# Revit family: BathrobeHolder-Single-Vitra-MinimaxSeries-A44787
name_source: partatom
category: Plumbing Fixtures
revit_build: Autodesk Revit 2017 (Build: 20160225_1515(x64)
units: mm (PartAtom-declared; Revit-internal decimal feet)

## family parameters
Cut with Voids When Loaded = No
Host = Face
OmniClass Number = 23.45.05.14.99
OmniClass Title = Other Sanitary Washing Plumbing Fixtures
Part Type = Normal
Room Calculation Point = No
Round Connector Dimension = Use Diameter
Shared = Yes

## types (4) — shared parameters
BIMobject category = Sanitary - Bathroom Accessories
CW Connection = No
Coating Material = Chrome
Color = Chrome
Default Elevation = 2000 mm  [stored 6.56168 ft]
Depth(mm) = 71 mm  [stored 0.23294 ft]
Description = Minimax Bathrobe Holder (Single)
Design country = Turkey
HW Connection = No
Height(mm) = 49 mm  [stored 0.160761 ft]
IFC Classification = Sanitary Terminal
Manufacturer = Vitra
Manufacturer name = Vitra
Masterformat 2014 Code = 01 52 19
Masterformat 2014 Description = Sanitary Facilities
MountingType = Wall-mounted
NBS Referans Code = 31-75
NBS Referans Description = Sanitary Accessories
Nominal height = 0.000
Nominal width = 0.000
OmniClass Code = 23-31 25 25
OmniClass Description = Towel Bars
Product Type = Built-in Bathrobe Holder
Product certification = https://vitraglobal.com
Product family = MinimaxSeries
Product group = Bathrobe Holder
Technical description = https://www.vitraglobal.com
UNSPSC Code = 301815
UNSPSC Description = Sanitary ware
URL = https://vitraglobal.com
Uniclass 1.4 Code = L721
Uniclass 1.4 Description = Sanitary equipment
Uniclass 2.0 Code = PR-31-75
Uniclass 2.0 Description = Sanitary Accessories
Uniclass 2015 Code = Pr_40_20_76_90
Uniclass 2015 Name = Towel rails
Uniformat II Description = FURNISHINGS
Warranty Period (Year) = 5 years
Weight Net (kg) = 0,215
Width(mm) = 44 mm  [stored 0.144357 ft]
Youtube = https://www.youtube.com
zero-valued in all types: CWFU, Cost, HWFU, WFU

## per-type parameters (varying)
| type | Article No. (default) | Brand | Model | Product SKU | Product data url | Product url |
| BathrobeHolder-Single-Vitra-MinimaxSeries-A44787 | A44787 |  | A44787 | A44787 |  | https://www.vitraglobal.com |
| BathrobeHolder-Single-Vitra-MinimaxSeries-A44787ART | A44787ART |  | A44787ART | A44787ART | https://www.vitraglobal.com |  |
| BathrobeHolder-Single-Vitra-MinimaxSeries-A44787EXP | A44787EXP | VitrA | A44787EXP | A44787EXP | https://www.vitraglobal.com |  |
| BathrobeHolder-Single-Vitra-MinimaxSeries-A44787VUK | A44787VUK | VitrA | A44787VUK | A44787VUK | https://www.vitraglobal.com |  |

note: [stored X ft] marks values corroborated as IEEE doubles in the binary element streams (Revit-internal decimal feet)

## geometry (parser evidence)
native form markers: Sweep x3
no freeform markers — native parametric forms only
